# Revit family: Drain_Sani_Flor_Receptor-Zurn-Z1995
name_source: partatom
category: Plumbing Fixtures
units: mm (PartAtom-declared; Revit-internal decimal feet)

## family parameters
Always vertical = Yes
Cut with Voids When Loaded = No
Maintain Annotation Orientation = No
OmniClass Number = 23.45.55.21
OmniClass Title = Drains (Wastes)
Part Type = Normal
Room Calculation Point = No
Round Connector Dimension = Use Radius
Shared = No
Work Plane-Based = No

## types (6) — shared parameters
Approx. Weight (Lbs) = 250.0 lb
Assembly Code = D2030300
CW Connection = No
Default Elevation = 20 "
Description = 24 X 16 [610 X 406] A.R.C. SANI-FLOR RECEPTOR 17 [432] SUMP DEPTH
Grate Open Area (Sq. In.) = 70 in²
HW Connection = No
Main Material = Iron - Zurn - Cast - White A.R.E Coated
Manufacturer = Zurn Water, LLC
Manufacurer Brand = Zurn
Modified Date = 02/06/2026
Product Documentation Link = https://files.zurn.com
Product Page URL = https://www.zurn.com
Product data url = https://www.bimobject.com
URL = www.zurn.com
Vent Connection = No
WFU = 1
Waste Connection = Yes
zero-valued in all types: CWFU, HWFU

## per-type parameters (varying)
| type | Body HT Dim 'E' | Grate Material | Length | Model | Pipe Size 'A' (Inner Diameter) | Pipe Size 'A' (Inner Radius) | Pipe Size 'A' (Nominal Diameter) | Pipe Size 'A' (Nominal Radius) | Pipe Size 'A' (Outer Diameter) | Pipe Size 'A' (Outer Radius) | Width | Z | ZN |
| Z1995-3 Inch No-Hub Outlet | 18.75 " | Iron - Zurn - Cast - White A.R.E Coated | 15.75 " | Z1995 | 3.068 " | 1.534 " | 3 " | 1.5 " | 3.5 " | 1.75 " | 23.75 " | Yes | No |
| Z1995-4 Inch No-Hub Outlet | 18.75 " | Iron - Zurn - Cast - White A.R.E Coated | 15.75 " | Z1995 | 4.028 " | 2.014 " | 4 " | 2 " | 4.5 " | 2.25 " | 23.75 " | Yes | No |
| Z1995-6 Inch No-Hub Outlet | 18.75 " | Iron - Zurn - Cast - White A.R.E Coated | 15.75 " | Z1995 | 6.065 " | 3.033 " | 6 " | 3 " | 6.625 " | 3.313 " | 23.75 " | Yes | No |
| ZN1995-3 Inch No-Hub Outlet | 19 " | Bronze - Zurn - Polished Nickel | 16.125 " | ZN1995 | 3.068 " | 1.534 " | 3 " | 1.5 " | 3.5 " | 1.75 " | 24.125 " | No | Yes |
| ZN1995-4 Inch No-Hub Outlet | 18.75 " | Bronze - Zurn - Polished Nickel | 16.125 " | ZN1995 | 4.028 " | 2.014 " | 4 " | 2 " | 4.5 " | 2.25 " | 24.125 " | No | Yes |
| ZN1995-6 Inch No-Hub Outlet | 18.75 " | Bronze - Zurn - Polished Nickel | 16.125 " | ZN1995 | 6.065 " | 3.033 " | 6 " | 3 " | 6.625 " | 3.313 " | 24.125 " | No | Yes |

## geometry (parser evidence)
native form markers: Blend x12, Sweep x5
no freeform markers — native parametric forms only
